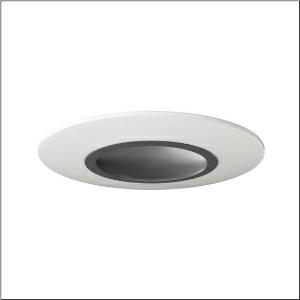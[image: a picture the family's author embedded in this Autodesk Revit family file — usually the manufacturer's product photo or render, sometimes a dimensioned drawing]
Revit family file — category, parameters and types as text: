
# Revit family: rondel_21_0md5307l1830
name_source: partatom
category: Lighting Fixtures
units: mm (PartAtom-declared; Revit-internal decimal feet)

## family parameters
Cut with Voids When Loaded = No
Host = Face
Light Source = No
Part Type = Normal
Room Calculation Point = No
Round Connector Dimension = Use Diameter
Shared = No

## types (1)
- Rondel 21 (1 x LED 3000K / CRI = 80 (unbekannt), 1800 lm, 3000K)
    Apparent Load = 18 VA
    CIE Flux Codes = 43 74 92 91 100
    Color Rendering = 80
    Color Temperature = 3000K
    Default Elevation = 1800 mm  [stored 5.90551 ft]
    Description = Rondel 21, wall and ceiling luminaire, of PC, opal, light emission: direct distribution, installation type: surface-mounted, LED, rated luminous flux: 1.800lm, luminous efficacy: 100lm/W, light colour: 830, colour temperature: 3000K, control gear: ECG, with terminal, 2-pole, mains connection: 220..240V, AC, 50/60Hz, rated input power: 18W, housing, round, of sheet steel, powder-coated, white, diameter: 380mm, height: 28mm, cover, of PC, graphite (RAL 7037), protection rating (complete): IP40, insulation class (complete): insulation class II (safety insulation), certification: CE, impact resistance: IK03, permissible operating ambient temperature: -20..+40°C, permissible storage temperature: -20..+80°C, packaging unit: 1 piece
    Height = 28 mm
    Lamp = 1 x LED 3000K / CRI >= 80 (unbekannt)
    Lamp Light Flux = 1800 lm
    Lamp count = 1
    Length = 380 mm
    Luminous efficacy = 100 lm/W
    Manufacturer = Siteco
    ModVariant = No
    Model = 0MD5307L1830
    Mounting Place = Ceiling
    Mounting Type = Surface mounted
    Number of Poles = 1
    OnlyDefault = Yes
    Power Factor = 1
    Product Name = Rondel 21
    Product group = wall and ceiling luminaire
    ProductGroupID = 301
    Protection Class = Protection class II
    Protection Degree = IP 40
    RLX_Detail_Level = 1
    RLX_Emergency_Light_Flux = 0 lm
    RLX_Emergency_Type = 0
    RLX_Emergency_Type_DB = No
    RlxData = <blob elided: 61581 chars, md5=7b4ac282>
    Socket = socket
    Standby Power = 0 W
    System Light Flux = 1800 lm
    System Power = 18 W
    Type Comments = Product without accessories
    Type Image = l_1005688.jpg
    URL = http://relux.com
    VarID = ---
    Voltage = 0 V
    Weight = 0.00 kg
    Width = 0 mm  [stored 0 ft]

note: [stored X ft] marks values corroborated as IEEE doubles in the binary element streams (Revit-internal decimal feet)

## geometry (parser evidence)
native form markers: Blend x4, Sweep x13
no freeform markers — native parametric forms only
